# Revit family: CENTUM Dachhalter für XL80
name_source: partatom
category: HLS-Bauteile
units: mm (PartAtom-declared; Revit-internal decimal feet)

## family parameters
Arbeitsebenenbasiert = Ja
Beim Laden mit Abzugskörper schneiden = Nein
Bemaßung runder Anschluss = Durchmesser verwenden
Beschriftungsausrichtung beibehalten = Nein
Gemeinsam genutzt = Ja
Immer vertikal = Nein
Klassifizierung = Keine
Raumberechnungspunkt = Nein
Teiletyp = Normal

## types (1)
- Dachhalter für CENTUM XL80
    Abmessung = 400 mm x 400 mm
    Artikelnummer = 166201001
    Beschreibung = Für Schienenkonstruktionen auf Flachdächern z.B. bei Lüftungskanälen, Dachgestellen
    Breite Platte = 400 mm  [stored 1.31234 ft]
    EAN = 4250928463555
    Fabrikat = MEFA
    Firma = MEFA Befestigungs- und Montagesysteme GmbH
    Gewicht = 3.01 kg
    Gewicht pro Bauteil = 3.01 kg
    Kurztext1 = Dachhalter CENTUM
    Kurztext2 = für XL 80
    Länge Platte = 400 mm  [stored 1.31234 ft]
    Material = Kunststoff
    Materialname = HDPE
    Mengeneinheit = St
    Profiltyp = XL 80
    Typ = Dachhalter für Centum XL80
    Typenkommentare = Das vormontierte Boden-Pad verhindert eine Beschädigung der Dachhaut durch Weichmacher. XL80 Profil wird zur Montage in den Dachhalter eingesteckt
    Vorgabe-Ansicht = 1219 mm
    für Profil = XL80
    max. Temperaturbeständigkeit = 80 °C
    max. zul. Last Druck = 10.00 kN
    min. Temperaturbeständigkeit = -40 oC
    vpe = 2

note: [stored X ft] marks values corroborated as IEEE doubles in the binary element streams (Revit-internal decimal feet)
